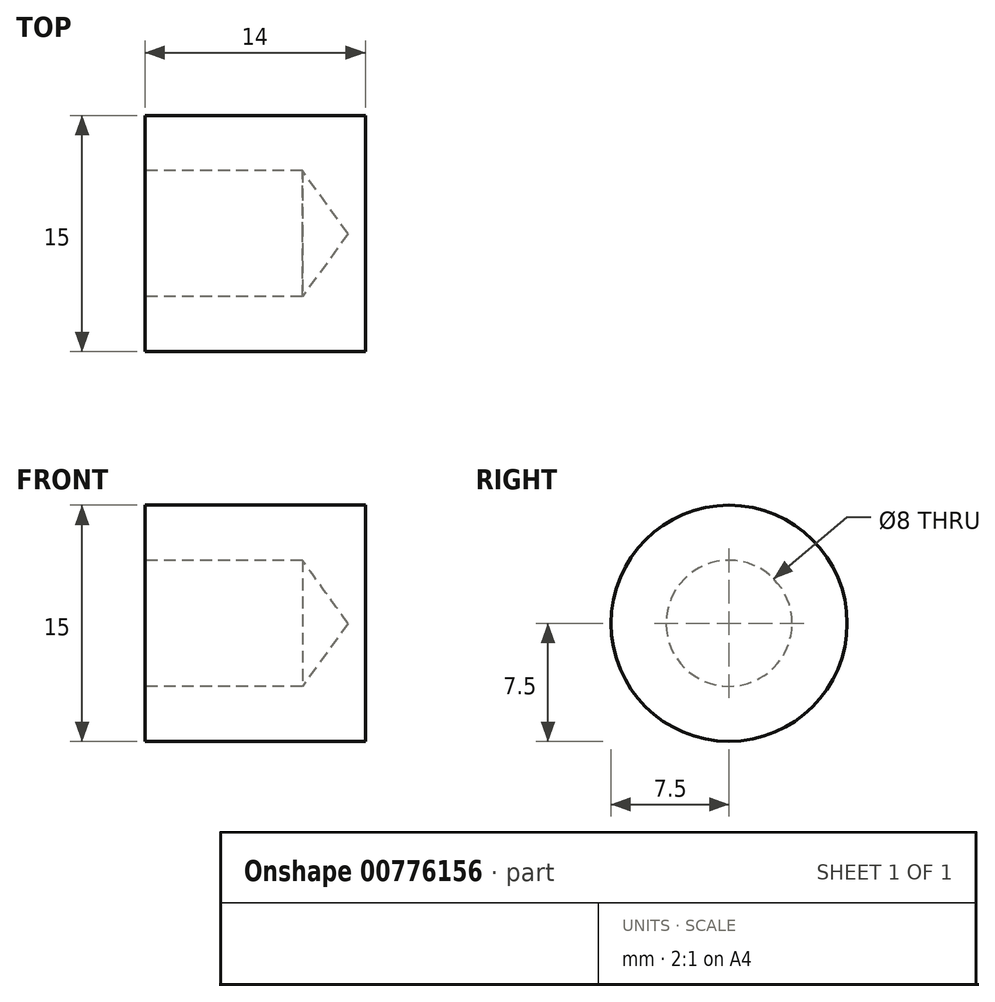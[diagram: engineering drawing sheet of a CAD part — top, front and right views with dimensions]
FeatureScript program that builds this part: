
annotation { "Feature Type Name" : "Feature", "Feature Type Description" : "" }
export const myFeature = defineFeature(function(context is Context, id is Id, definition is map)
    precondition{}
    {
        {
            var Q0;
            Q0=qCreatedBy(makeId("Front.planeOp"),FACE);
            var sketch = newSketch(context, id + "F0", { "sketchPlane" : qUnion([Q0])});
            skLineSegment(sketch, "E0.bottom", {"start": v(0, 0) * mm, "end": v(14, 0) * mm});
            skLineSegment(sketch, "E0.top", {"start": v(0, 7.5) * mm, "end": v(14, 7.5) * mm});
            skLineSegment(sketch, "E0.left", {"start": v(0, 0) * mm, "end": v(0, 7.5) * mm});
            skLineSegment(sketch, "E0.right", {"start": v(14, 0) * mm, "end": v(14, 7.5) * mm});
            skLineSegment(sketch, "E1.bottom", {"start": v(0, 0) * mm, "end": v(10, 0) * mm});
            skLineSegment(sketch, "E1.top", {"start": v(0, 4) * mm, "end": v(10, 4) * mm});
            skLineSegment(sketch, "E1.left", {"start": v(0, 0) * mm, "end": v(0, 4) * mm});
            skLineSegment(sketch, "E1.right", {"start": v(10, 0) * mm, "end": v(10, 4) * mm});
            skLineSegment(sketch, "E2", {"start": v(10, 4) * mm, "end": v(12.9, 0) * mm});
            skSolve(sketch);
        }
        {
            var Q0;
            {var subQ2=sQuery(id+"F0.wireOp",EDGE,"E0.top");Q0=makeQuery(id+"F0.imprint","IMPRINT",FACE,{"disambiguationData":[TD([[makeQuery(id+"F0.imprint","IMPRINT",EDGE,{"derivedFrom":subQ2}),-1.0]])]});}
            var Q1;
            Q1=sQuery(id+"F0.wireOp",EDGE,"E1.bottom");
            revolve(context, id + "F1", {"surfaceOperationType" : NewSurfaceOperationType.NEW, "entities" : qUnion([Q0]), "axis" : qUnion([Q1]), "revolveType" : RevolveType.FULL});
        }
    });
